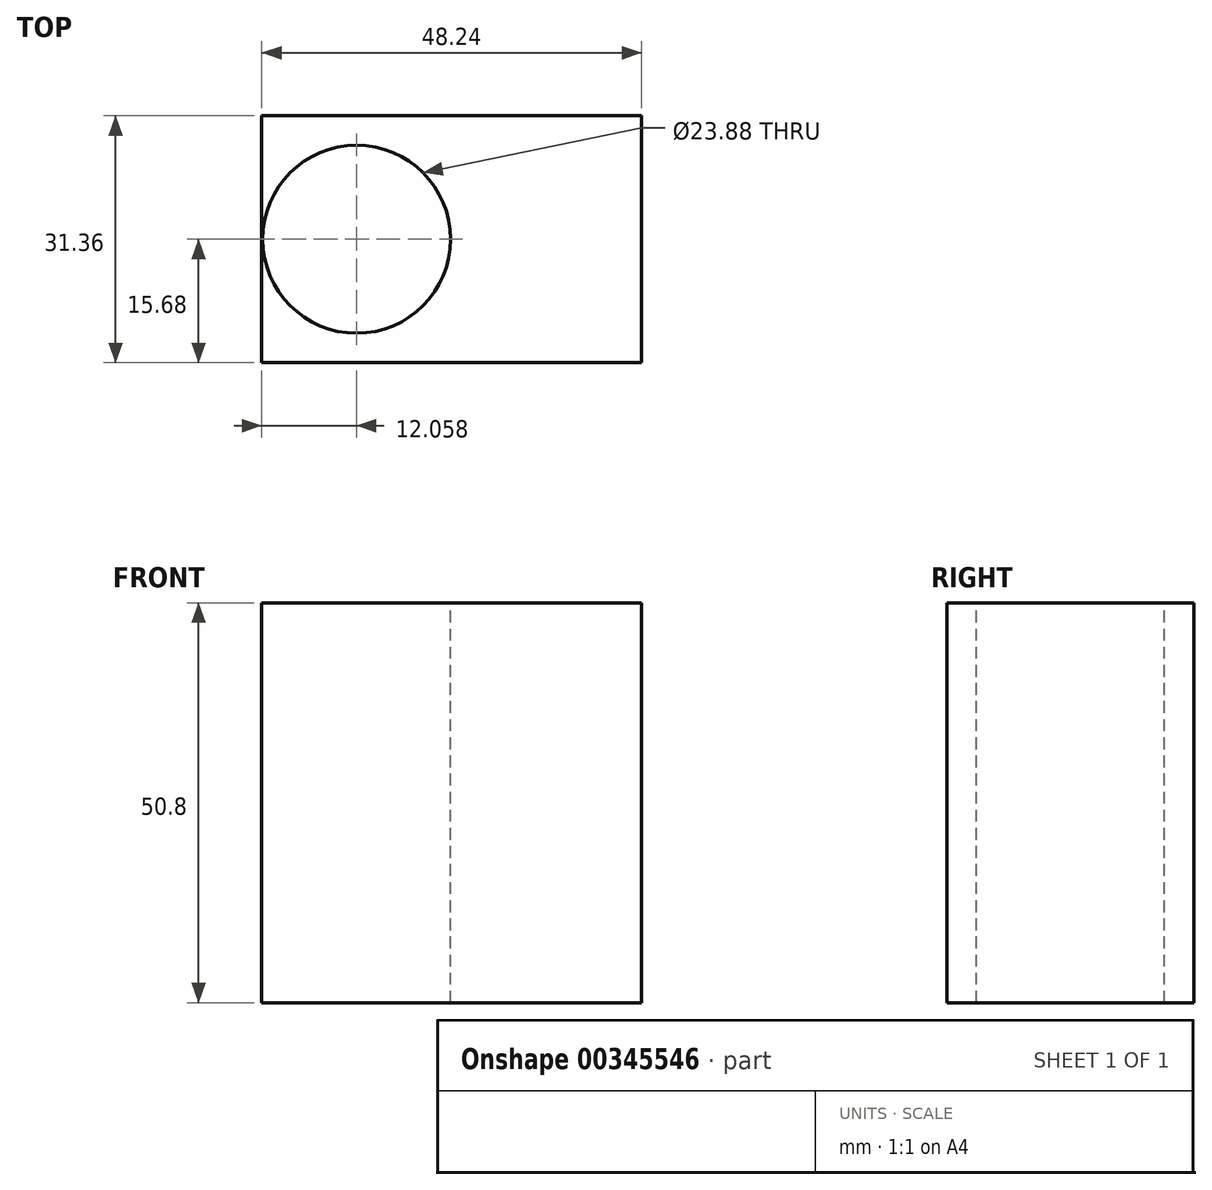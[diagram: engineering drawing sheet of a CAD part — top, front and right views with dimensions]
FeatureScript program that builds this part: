
annotation { "Feature Type Name" : "Feature", "Feature Type Description" : "" }
export const myFeature = defineFeature(function(context is Context, id is Id, definition is map)
    precondition{}
    {
        {
            var Q0;
            Q0=qCreatedBy(makeId("Top.planeOp"),FACE);
            var sketch = newSketch(context, id + "F0", { "sketchPlane" : qUnion([Q0])});
            skLineSegment(sketch, "E0.bottom", {"start": v(24.12, 15.68) * mm, "end": v(-24.12, 15.68) * mm});
            skLineSegment(sketch, "E0.top", {"start": v(24.12, -15.68) * mm, "end": v(-24.12, -15.68) * mm});
            skLineSegment(sketch, "E0.left", {"start": v(24.12, 15.68) * mm, "end": v(24.12, -15.68) * mm});
            skLineSegment(sketch, "E0.right", {"start": v(-24.12, 15.68) * mm, "end": v(-24.12, -15.68) * mm});
            skPoint(sketch, "E0.middle", {"position": v(0, 0) * mm});
            skSolve(sketch);
        }
        {
            var Q0;
            Q0 = qSketchRegion(id + "F0", true);
            extrude(context, id + "F1", {"entities" : qUnion([Q0]), "depth" : 50.8 * mm});
        }
        {
            var Q0;
            Q0=makeQuery(id+"F1.opExtrude","CAP_FACE",FACE,{"disambiguationData":[OSD([sQuery(id+"F0.wireOp",EDGE,"E0.bottom"),sQuery(id+"F0.wireOp",EDGE,"E0.top"),sQuery(id+"F0.wireOp",EDGE,"E0.left"),sQuery(id+"F0.wireOp",EDGE,"E0.right")])],"isStart":false});
            var sketch = newSketch(context, id + "F2", { "sketchPlane" : qUnion([Q0])});
            skLineSegment(sketch, "E1", {"start": v(0, 0) * mm, "end": v(-24.12, 0) * mm});
            skCircle(sketch, "E2", {"center": v(-12.06, 0) * mm, "radius": 12 * mm});
            skSolve(sketch);
        }
        {
            var Q0;
            Q0=sQuery(id+"F2.wireOp",VERTEX,"E2.center");
            var Q1;
            Q1=makeQuery(id+"F1.opExtrude","SWEPT_BODY",BODY,{"disambiguationData":[OSD([sQuery(id+"F0.wireOp",EDGE,"E0.bottom"),sQuery(id+"F0.wireOp",EDGE,"E0.top"),sQuery(id+"F0.wireOp",EDGE,"E0.left"),sQuery(id+"F0.wireOp",EDGE,"E0.right")])]});
            hole(context, id + "F3", {"style" : HoleStyle.SIMPLE, "endStyle" : HoleEndStyle.THROUGH, "holeDiameter" : 23.88 * mm, "isTappedThrough" : true, "tappedDepth" : 12.7 * mm, "tapClearance" : 3, "locations" : qUnion([Q0]), "scope" : qUnion([Q1])});
        }
    });
